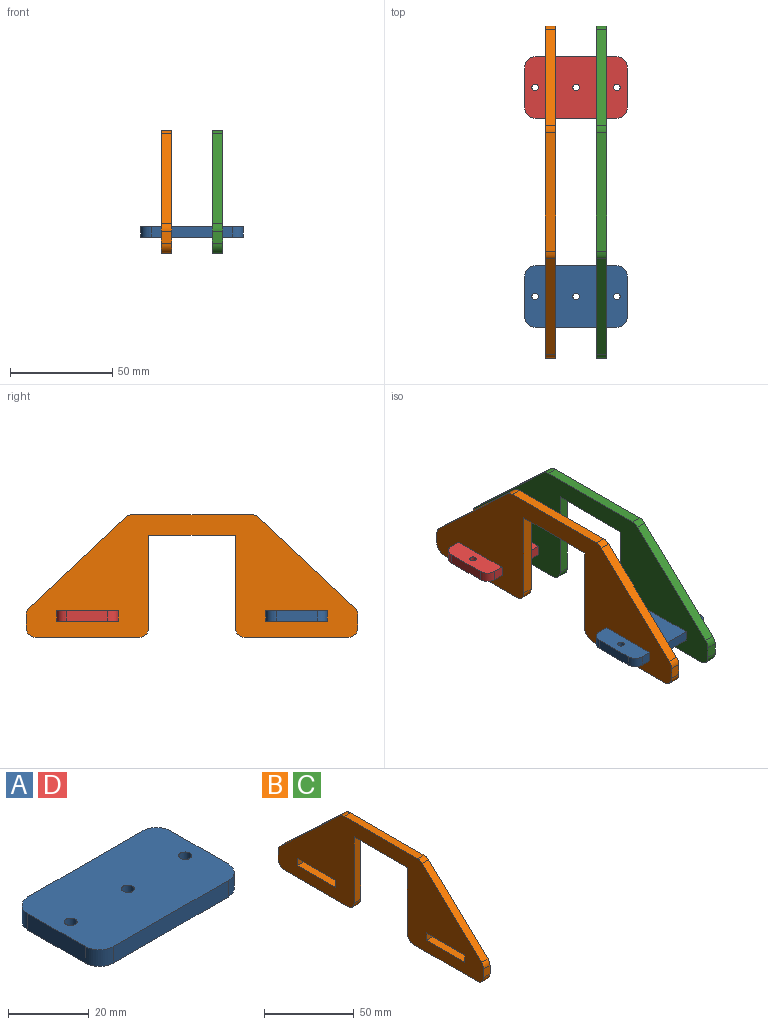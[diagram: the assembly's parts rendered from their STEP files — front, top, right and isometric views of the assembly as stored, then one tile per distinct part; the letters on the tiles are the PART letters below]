
ASSEMBLY  parts=4 mates=3
PART A: 13 faces, bbox 50x30x5 mm
  f0: plane 40x5mm, normal (0,-1,0), area 200mm2, adj f1,f8,f11,f12
  f1: cylinder r=5mm len=5mm, axis (0,0,-1), area 39.3mm2, adj f0,f2,f11,f12
  f2: plane 20x5mm, normal (1,0,0), area 100mm2, adj f1,f3,f11,f12
  f3: cylinder r=5mm len=5mm, axis (0,0,-1), area 39.3mm2, adj f2,f4,f11,f12
  f4: plane 40x5mm, normal (0,1,0), area 200mm2, adj f3,f5,f11,f12
  f5: cylinder r=5mm len=5mm, axis (0,0,-1), area 39.3mm2, adj f4,f6,f11,f12
  f6: plane 20x5mm, normal (-1,0,0), area 100mm2, adj f5,f8,f11,f12
  f7: cylinder r=1.6mm len=5mm, axis (0,0,-1), area 50.3mm2, adj f11,f12
  f8: cylinder r=5mm len=5mm, axis (0,0,-1), area 39.3mm2, adj f0,f6,f11,f12
  f9: cylinder r=1.6mm len=5mm, axis (0,0,-1), area 50.3mm2, adj f11,f12
  f10: cylinder r=1.6mm len=5mm, axis (0,0,-1), area 50.3mm2, adj f11,f12
  f11: plane 50x30mm, normal (0,0,1), area 1454.4mm2, adj f0,f1,f2,f3,f4,f5,f6,f7
  f12: plane 50x30mm, normal (0,0,-1), area 1454.4mm2, adj f0,f1,f2,f3,f4,f5,f6,f7
PART B: 28 faces, bbox 5x162x60 mm
  f0: plane 5x5mm, normal (0,-1,0), area 25mm2, adj f1,f25,f26,f27
  f1: plane 30x5mm, normal (0,0,1), area 150mm2, adj f0,f2,f26,f27
  f2: plane 5x5mm, normal (0,1,0), area 25mm2, adj f1,f25,f26,f27
  f3: plane 5x5mm, normal (0,1,0), area 25mm2, adj f4,f23,f26,f27
  f4: plane 30x5mm, normal (0,0,-1), area 150mm2, adj f3,f5,f26,f27
  f5: plane 5x5mm, normal (0,-1,0), area 25mm2, adj f4,f23,f26,f27
  f6: plane 58.04x5mm, normal (0,0,1), area 290.2mm2, adj f7,f24,f26,f27
  f7: cylinder r=5mm len=5mm, axis (-1,0,0), area 18.9mm2, adj f6,f8,f26,f27
  f8: plane 46.98x44.16mm, normal (0,-0.68,0.73), area 322.4mm2, adj f7,f9,f26,f27
  f9: cylinder r=5mm len=5mm, axis (-1,0,0), area 20.4mm2, adj f8,f10,f26,f27
  f10: plane 5.84x5mm, normal (0,-1,0), area 29.2mm2, adj f9,f11,f26,f27
  f11: cylinder r=5mm len=5mm, axis (-1,0,0), area 39.3mm2, adj f10,f12,f26,f27
  f12: plane 50x5mm, normal (0,0,-1), area 250mm2, adj f11,f13,f26,f27
  f13: cylinder r=5mm len=5mm, axis (-1,0,0), area 39.3mm2, adj f12,f14,f26,f27
  f14: plane 45x5mm, normal (0,1,0), area 225mm2, adj f13,f15,f26,f27
  f15: plane 42x5mm, normal (0,0,-1), area 210mm2, adj f14,f16,f26,f27
  f16: plane 45x5mm, normal (0,-1,0), area 225mm2, adj f15,f17,f26,f27
  f17: cylinder r=5mm len=5mm, axis (-1,0,0), area 39.3mm2, adj f16,f18,f26,f27
  f18: plane 50x5mm, normal (0,0,-1), area 250mm2, adj f17,f19,f26,f27
  f19: cylinder r=5mm len=5mm, axis (-1,0,0), area 39.3mm2, adj f18,f20,f26,f27
  f20: plane 5.84x5mm, normal (0,1,0), area 29.2mm2, adj f19,f21,f26,f27
  f21: cylinder r=5mm len=5mm, axis (-1,0,0), area 20.4mm2, adj f20,f22,f26,f27
  f22: plane 46.98x44.16mm, normal (0,0.68,0.73), area 322.4mm2, adj f21,f24,f26,f27
  f23: plane 30x5mm, normal (0,0,1), area 150mm2, adj f3,f5,f26,f27
  f24: cylinder r=5mm len=5mm, axis (-1,0,0), area 18.9mm2, adj f6,f22,f26,f27
  f25: plane 30x5mm, normal (0,0,-1), area 150mm2, adj f0,f2,f26,f27
  f26: plane 162x60mm, normal (1,0,0), area 4946.4mm2, adj f0,f1,f2,f3,f4,f5,f6,f7
  f27: plane 162x60mm, normal (-1,0,0), area 4946.4mm2, adj f0,f1,f2,f3,f4,f5,f6,f7
PART C: same geometry as B
PART D: same geometry as A
PLACE A t=(14.8,-64.48,24.48)mm
PLACE B t=(-0.2,-34.48,16.48)mm
PLACE C t=(24.8,-34.48,16.48)mm
PLACE D t=(14.8,37.52,24.48)mm
MATE fastened D.f11 <-> C.f25  axis (0,0,1) through (39.8,37.52,29.48)mm
MATE fastened D.f11 <-> B.f25  axis (0,0,1) through (-10.2,37.52,29.48)mm
MATE fastened A.f11 <-> C.f4  axis (0,0,1) through (39.8,-64.48,29.48)mm
